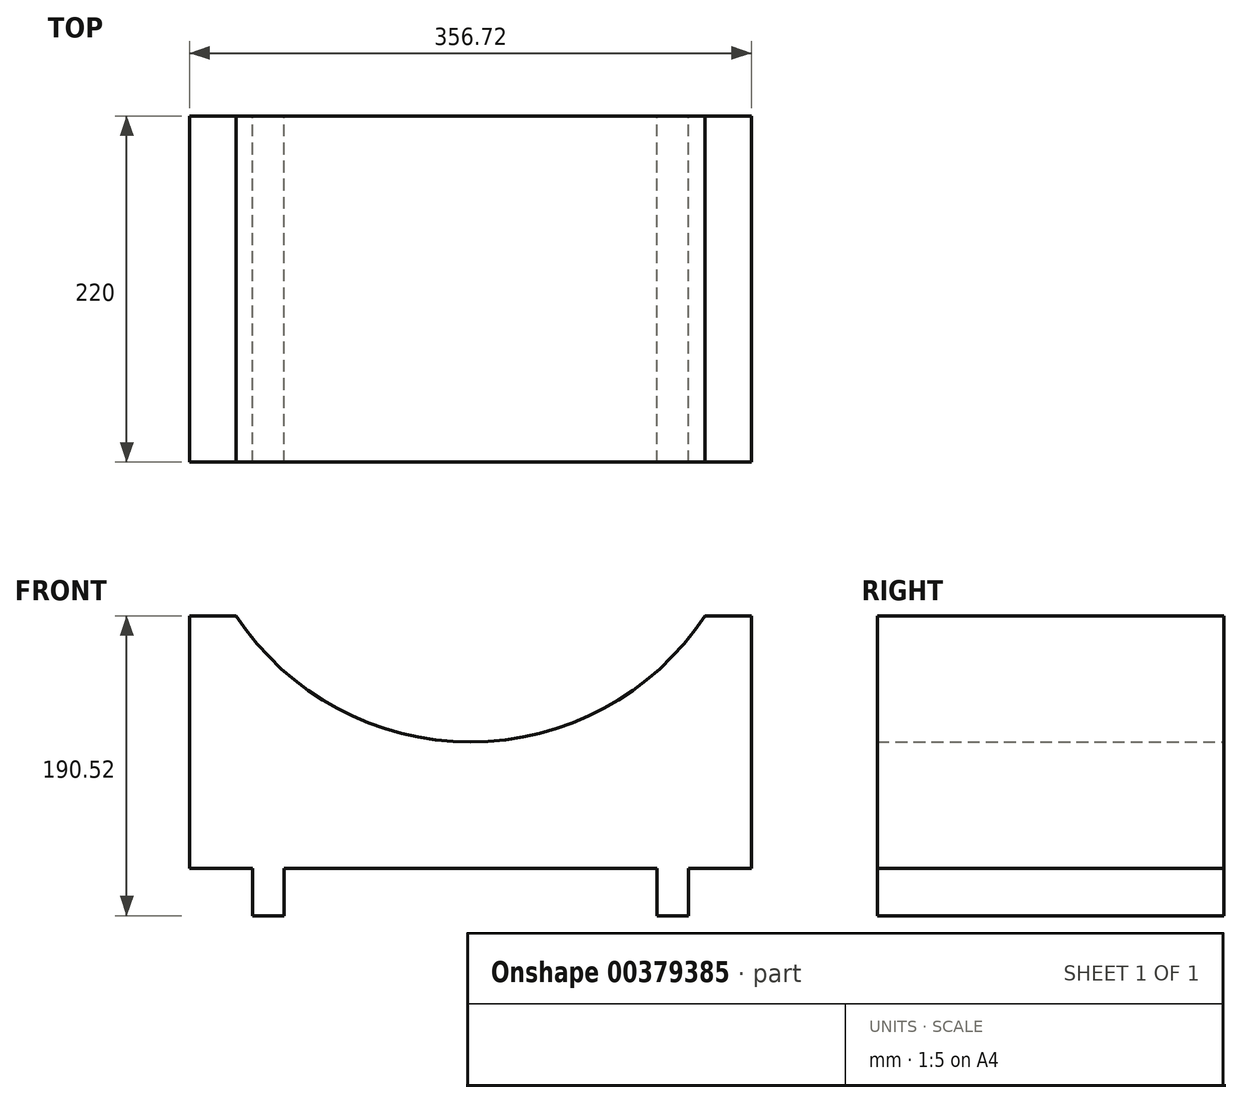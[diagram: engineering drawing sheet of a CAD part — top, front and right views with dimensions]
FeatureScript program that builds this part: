
annotation { "Feature Type Name" : "Feature", "Feature Type Description" : "" }
export const myFeature = defineFeature(function(context is Context, id is Id, definition is map)
    precondition{}
    {
        {
            var Q0;
            Q0=qCreatedBy(makeId("Front.planeOp"),FACE);
            var sketch = newSketch(context, id + "F0", { "sketchPlane" : qUnion([Q0])});
            skLineSegment(sketch, "E0.bottom", {"start": v(-178.36, -80.26) * mm, "end": v(-138.36, -80.26) * mm});
            skLineSegment(sketch, "E0.top", {"start": v(-178.36, 80.26) * mm, "end": v(-148.96, 80.26) * mm});
            skLineSegment(sketch, "E0.left", {"start": v(-178.36, -80.26) * mm, "end": v(-178.36, 80.26) * mm});
            skLineSegment(sketch, "E0.right", {"start": v(178.36, -80.26) * mm, "end": v(178.36, 80.26) * mm});
            skPoint(sketch, "E0.middle", {"position": v(0, 0) * mm});
            skArc(sketch, "E1", {"start": v(-148.96, 80.26) * mm, "mid": v(0, 0) * mm, "end": v(148.96, 80.26) * mm});
            skLineSegment(sketch, "E2.top", {"start": v(-138.36, -110.26) * mm, "end": v(-118.36, -110.26) * mm});
            skLineSegment(sketch, "E2.left", {"start": v(-138.36, -80.26) * mm, "end": v(-138.36, -110.26) * mm});
            skLineSegment(sketch, "E2.right", {"start": v(-118.36, -80.26) * mm, "end": v(-118.36, -110.26) * mm});
            skLineSegment(sketch, "E3.top", {"start": v(118.36, -110.26) * mm, "end": v(138.36, -110.26) * mm});
            skLineSegment(sketch, "E3.left", {"start": v(118.36, -80.26) * mm, "end": v(118.36, -110.26) * mm});
            skLineSegment(sketch, "E3.right", {"start": v(138.36, -80.26) * mm, "end": v(138.36, -110.26) * mm});
            skLineSegment(sketch, "E4.trimOffspring", {"start": v(-118.36, -80.26) * mm, "end": v(118.36, -80.26) * mm});
            skLineSegment(sketch, "E5.trimOffspring", {"start": v(138.36, -80.26) * mm, "end": v(178.36, -80.26) * mm});
            skLineSegment(sketch, "E6.trimOffspring", {"start": v(148.96, 80.26) * mm, "end": v(178.36, 80.26) * mm});
            skSolve(sketch);
        }
        {
            var Q0;
            Q0=makeQuery(id+"F0.imprint","IMPRINT",FACE,{"disambiguationData":[TD([[makeQuery(id+"F0.imprint","IMPRINT",EDGE,{"derivedFrom":sQuery(id+"F0.wireOp",EDGE,"E0.bottom")}),1.0]])]});
            extrude(context, id + "F1", {"entities" : qUnion([Q0]), "depth" : 220 * mm});
        }
        {
            var Q0;
            Q0=makeQuery(id+"F1.opExtrude","SWEPT_FACE",FACE,{"disambiguationData":[OSD([sQuery(id+"F0.wireOp",EDGE,"E0.right")])]});
            var sketch = newSketch(context, id + "F2", { "sketchPlane" : qUnion([Q0])});
            skLineSegment(sketch, "E7", {"start": v(-259.1, -125.26) * mm, "end": v(123.92, -125.26) * mm, "construction": true});
            skLineSegment(sketch, "E8", {"start": v(-186, 21.02) * mm, "end": v(-186, -181.08) * mm, "construction": true});
            skCircle(sketch, "E9", {"center": v(-203, -125.26) * mm, "radius": 15 * mm});
            skCircle(sketch, "E10.MirrorC", {"center": v(-169, -125.26) * mm, "radius": 15 * mm});
            skCircle(sketch, "E11.MirrorC", {"center": v(-237, -125.26) * mm, "radius": 15 * mm});
            skLineSegment(sketch, "E12", {"start": v(-152, -35.27) * mm, "end": v(-152, -183.36) * mm, "construction": true});
            skCircle(sketch, "E13.MirrorC", {"center": v(-67, -125.26) * mm, "radius": 15 * mm});
            skCircle(sketch, "E14.MirrorC", {"center": v(-101, -125.26) * mm, "radius": 15 * mm});
            skCircle(sketch, "E15.MirrorC", {"center": v(-135, -125.26) * mm, "radius": 15 * mm});
            skLineSegment(sketch, "E16", {"start": v(-50, 0) * mm, "end": v(-50, -202.77) * mm, "construction": true});
            skCircle(sketch, "E17.MirrorC", {"center": v(137, -125.26) * mm, "radius": 15 * mm});
            skCircle(sketch, "E18.MirrorC", {"center": v(103, -125.26) * mm, "radius": 15 * mm});
            skCircle(sketch, "E19.MirrorC", {"center": v(69, -125.26) * mm, "radius": 15 * mm});
            skCircle(sketch, "E20.MirrorC", {"center": v(35, -125.26) * mm, "radius": 15 * mm});
            skCircle(sketch, "E21.MirrorC", {"center": v(1, -125.26) * mm, "radius": 15 * mm});
            skCircle(sketch, "E22.MirrorC", {"center": v(-33, -125.26) * mm, "radius": 15 * mm});
            skLineSegment(sketch, "E23.MirrorCS", {"start": v(86, 21.02) * mm, "end": v(86, -181.08) * mm, "construction": true});
            skLineSegment(sketch, "E24", {"start": v(-254, 50.17) * mm, "end": v(-254, -227.48) * mm, "construction": true});
            skCircle(sketch, "E25.MirrorC", {"center": v(-645, -125.26) * mm, "radius": 15 * mm});
            skCircle(sketch, "E26.MirrorC", {"center": v(-611, -125.26) * mm, "radius": 15 * mm});
            skCircle(sketch, "E27.MirrorC", {"center": v(-577, -125.26) * mm, "radius": 15 * mm});
            skCircle(sketch, "E28.MirrorC", {"center": v(-543, -125.26) * mm, "radius": 15 * mm});
            skCircle(sketch, "E29.MirrorC", {"center": v(-509, -125.26) * mm, "radius": 15 * mm});
            skCircle(sketch, "E30.MirrorC", {"center": v(-475, -125.26) * mm, "radius": 15 * mm});
            skCircle(sketch, "E31.MirrorC", {"center": v(-441, -125.26) * mm, "radius": 15 * mm});
            skCircle(sketch, "E32.MirrorC", {"center": v(-407, -125.26) * mm, "radius": 15 * mm});
            skCircle(sketch, "E33.MirrorC", {"center": v(-373, -125.26) * mm, "radius": 15 * mm});
            skCircle(sketch, "E34.MirrorC", {"center": v(-339, -125.26) * mm, "radius": 15 * mm});
            skCircle(sketch, "E35.MirrorC", {"center": v(-305, -125.26) * mm, "radius": 15 * mm});
            skCircle(sketch, "E36.MirrorC", {"center": v(-271, -125.26) * mm, "radius": 15 * mm});
            skSolve(sketch);
        }
        {
            var Q0;
            Q0=sQuery(id+"F2.wireOp",EDGE,"E26.MirrorC");
            var Q1;
            Q1=sQuery(id+"F2.wireOp",EDGE,"E25.MirrorC");
            var Q2;
            Q2=sQuery(id+"F2.wireOp",EDGE,"E27.MirrorC");
            var Q3;
            Q3=sQuery(id+"F2.wireOp",EDGE,"E28.MirrorC");
            var Q4;
            Q4=sQuery(id+"F2.wireOp",EDGE,"E29.MirrorC");
            var Q5;
            Q5=sQuery(id+"F2.wireOp",EDGE,"E30.MirrorC");
            var Q6;
            Q6=sQuery(id+"F2.wireOp",EDGE,"E31.MirrorC");
            var Q7;
            Q7=sQuery(id+"F2.wireOp",EDGE,"E32.MirrorC");
            var Q8;
            Q8=sQuery(id+"F2.wireOp",EDGE,"E33.MirrorC");
            var Q9;
            Q9=sQuery(id+"F2.wireOp",EDGE,"E34.MirrorC");
            var Q10;
            Q10=sQuery(id+"F2.wireOp",EDGE,"E35.MirrorC");
            var Q11;
            Q11=sQuery(id+"F2.wireOp",EDGE,"E36.MirrorC");
            var Q12;
            Q12=sQuery(id+"F2.wireOp",EDGE,"E11.MirrorC");
            var Q13;
            Q13=sQuery(id+"F2.wireOp",EDGE,"E9");
            var Q14;
            Q14=sQuery(id+"F2.wireOp",EDGE,"E10.MirrorC");
            var Q15;
            Q15=sQuery(id+"F2.wireOp",EDGE,"E15.MirrorC");
            var Q16;
            Q16=sQuery(id+"F2.wireOp",EDGE,"E14.MirrorC");
            var Q17;
            Q17=sQuery(id+"F2.wireOp",EDGE,"E13.MirrorC");
            var Q18;
            Q18=sQuery(id+"F2.wireOp",EDGE,"E22.MirrorC");
            var Q19;
            Q19=sQuery(id+"F2.wireOp",EDGE,"E21.MirrorC");
            var Q20;
            Q20=sQuery(id+"F2.wireOp",EDGE,"E20.MirrorC");
            var Q21;
            Q21=sQuery(id+"F2.wireOp",EDGE,"E19.MirrorC");
            var Q22;
            Q22=sQuery(id+"F2.wireOp",EDGE,"E18.MirrorC");
            var Q23;
            Q23=sQuery(id+"F2.wireOp",EDGE,"E17.MirrorC");
            var Q24;
            Q24=makeQuery(id+"F1.opExtrude","SWEPT_FACE",FACE,{"disambiguationData":[OSD([sQuery(id+"F0.wireOp",EDGE,"E0.left")])]});
            extrude(context, id + "F3", {"bodyType" : ToolBodyType.SURFACE, "surfaceEntities" : qUnion([Q0, Q1, Q2, Q3, Q4, Q5, Q6, Q7, Q8, Q9, Q10, Q11, Q12, Q13, Q14, Q15, Q16, Q17, Q18, Q19, Q20, Q21, Q22, Q23]), "endBound" : BoundingType.UP_TO_SURFACE, "oppositeDirection" : true, "endBoundEntityFace" : qUnion([Q24]), "depth" : 380 * mm});
        }
    });
